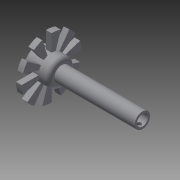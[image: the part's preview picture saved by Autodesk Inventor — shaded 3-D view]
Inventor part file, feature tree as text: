
AUTODESK INVENTOR PART (.ipt)
format: ipt  version: 2015 (Build 190159000, 159)  size: 225,280 bytes
history: native  units: mm
features: sketch x15, extrude x10, plane x5, pattern_circular x2, sweep x2, fillet x1
ambient origin geometry x8: Origin, YZ Plane, XZ Plane, XY Plane, X Axis, Y Axis, Z Axis, Center Point
bodies: Solid1 (feature_tree)
feature tree (35):
  extrude  "Extrusion1"  Depth=3.141593mm
  pattern_circular  "Circular Pattern1"  Count=10 Angle=360.0deg
  plane  "Work Plane1"
  extrude  "Extrusion2"  Depth=14.0mm
  extrude  "Extrusion3"  Depth=3.0mm TaperAngle=0.0deg
  extrude  "Extrusion4"  Depth=8.2mm
  extrude  "Extrusion5"  Depth=1.85mm
  extrude  "Extrusion6"  Depth=1.0mm TaperAngle=0.0deg
  extrude  "Extrusion7"  Depth=5.8mm
  fillet  "Fillet1"  Radius=40.0mm
  extrude  "Extrusion8"  [1 undecoded]
  extrude  "Extrusion9"  TaperAngle=0.0deg  [1 undecoded]
  plane  "Work Plane2"
  sketch  "Sketch10"  dims[d31=2.5mm d32=0.0mm d33=0.0mm]
  plane  "Work Plane3"
  sweep  "Sweep1"
  plane  "Work Plane4"
  sketch  "Sketch12"  dims[d36=3.0mm d37=0.0mm d38=0.0mm]
  plane  "Work Plane5"
  sweep  "Sweep2"
  sketch  "Sketch14"
  extrude  "Extrusion10"  Depth=5.0mm TaperAngle=0.0deg
  pattern_circular  "Circular Pattern2"  Count=3 Angle=360.0deg
  sketch  "Sketch1"  dims[d0=16.0mm d1=3.141593mm]
  sketch  "Sketch2"  dims[d3=3.0mm d4=0.0mm d5=100.0mm d6=360.0deg]
  sketch  "Sketch3"  dims[d8=3.0mm d9=14.0mm]
  sketch  "Sketch4"  dims[d10=4.5mm d11=0.0mm d12=3.0mm d13=0.0mm]
  sketch  "Sketch5"  dims[d14=4.5mm d15=0.0mm d16=8.2mm]
  sketch  "Sketch6"  dims[d17=40.0mm d18=0.0mm d19=1.85mm]
  sketch  "Sketch7"  dims[d20=9.0mm d21=0.0mm d22=1.0mm d23=0.0mm]
  sketch  "Sketch8"  dims[d24=2.0mm d25=5.8mm d26=40.0mm d27=0.0mm]
  sketch  "Sketch9"  dims[d28=4.0mm d29=0.0mm d30=-2.0mm]
  sketch  "Sketch11"  dims[d34=-2.0mm d35=2.0mm]
  sketch  "Sketch13"  dims[d39=1.6mm d40=5.0mm d41=0.0mm d42=30.0mm d43=360.0deg]
  sketch  "Sketch15"
note: 2 required parameter values undecoded (feature->parameter linkage not recoverable at this tier; creation-order binding heuristic only, values carry confidence <= 0.55)
